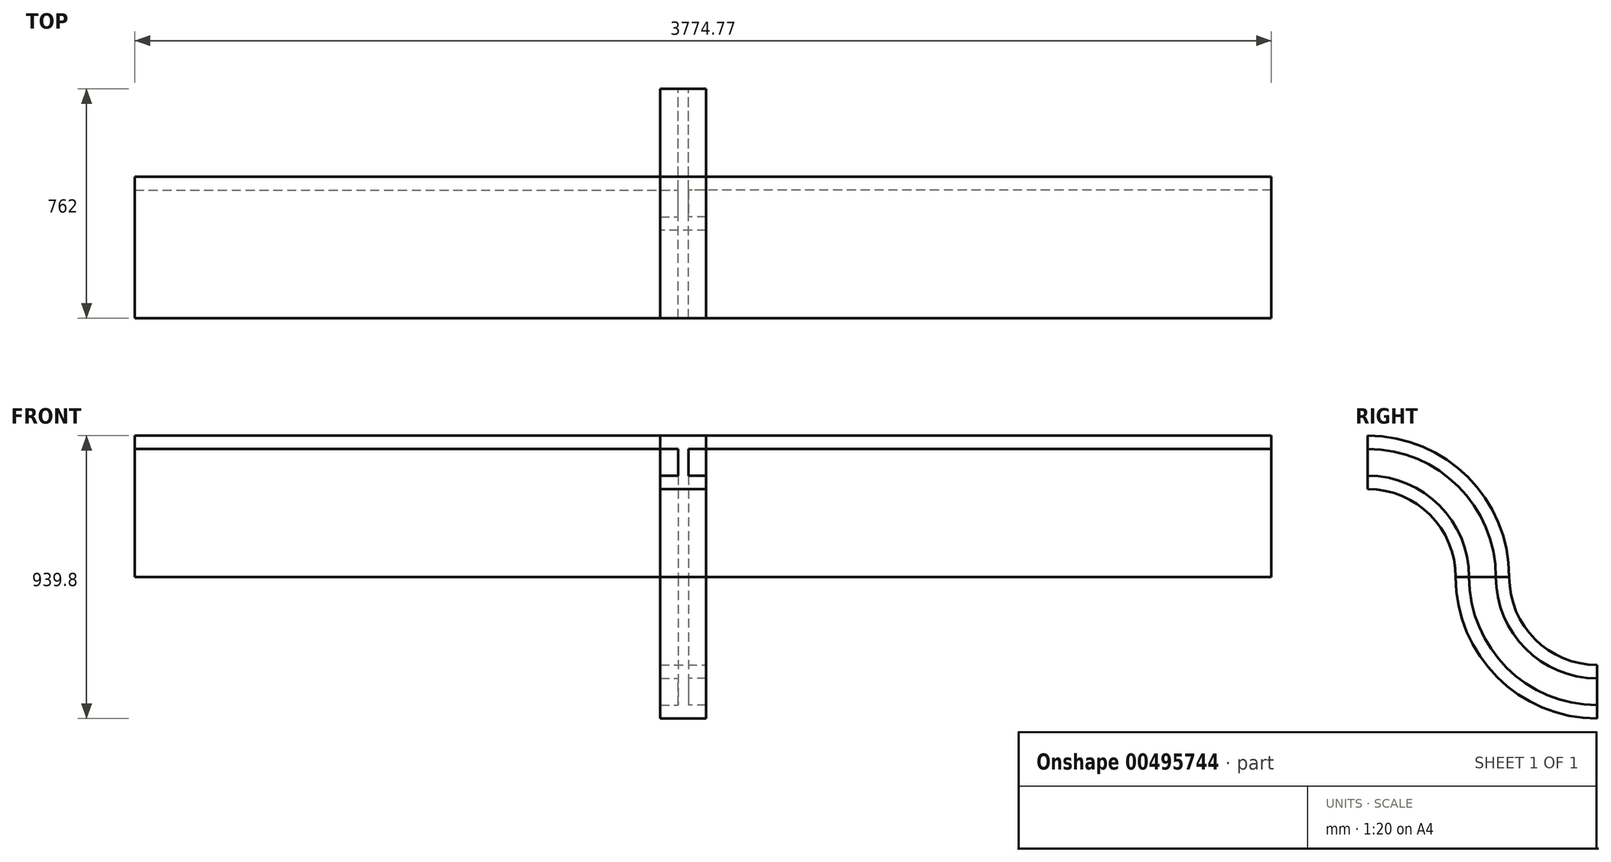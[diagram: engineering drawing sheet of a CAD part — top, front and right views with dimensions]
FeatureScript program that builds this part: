
annotation { "Feature Type Name" : "Feature", "Feature Type Description" : "" }
export const myFeature = defineFeature(function(context is Context, id is Id, definition is map)
    precondition{}
    {
        {
            var Q0;
            Q0=qCreatedBy(makeId("Front.planeOp"),FACE);
            var sketch = newSketch(context, id + "F0", { "sketchPlane" : qUnion([Q0])});
            skLineSegment(sketch, "E0", {"start": v(0, 88.9) * mm, "end": v(76.2, 88.9) * mm});
            skLineSegment(sketch, "E1", {"start": v(76.2, 88.9) * mm, "end": v(76.2, 44.45) * mm});
            skLineSegment(sketch, "E2", {"start": v(76.2, 44.45) * mm, "end": v(17.37, 44.45) * mm});
            skLineSegment(sketch, "E3", {"start": v(0, 88.9) * mm, "end": v(0, -88.9) * mm, "construction": true});
            skLineSegment(sketch, "E4", {"start": v(-17.37, 0) * mm, "end": v(17.37, 0) * mm, "construction": true});
            skLineSegment(sketch, "E5", {"start": v(17.37, 0) * mm, "end": v(17.37, 44.45) * mm});
            skLineSegment(sketch, "E6.MirrorCS", {"start": v(0, 88.9) * mm, "end": v(-76.2, 88.9) * mm});
            skLineSegment(sketch, "E7.MirrorCS", {"start": v(-76.2, 88.9) * mm, "end": v(-76.2, 44.45) * mm});
            skLineSegment(sketch, "E8.MirrorCS", {"start": v(-17.37, 0) * mm, "end": v(-17.37, 44.45) * mm});
            skLineSegment(sketch, "E9.MirrorCS", {"start": v(-76.2, 44.45) * mm, "end": v(-17.37, 44.45) * mm});
            skLineSegment(sketch, "E10.MirrorCS", {"start": v(0, -88.9) * mm, "end": v(-76.2, -88.9) * mm});
            skLineSegment(sketch, "E11.MirrorCS", {"start": v(-76.2, -88.9) * mm, "end": v(-76.2, -44.45) * mm});
            skLineSegment(sketch, "E12.MirrorCS", {"start": v(-76.2, -44.45) * mm, "end": v(-17.37, -44.45) * mm});
            skLineSegment(sketch, "E13.MirrorCS", {"start": v(-17.37, 0) * mm, "end": v(-17.37, -44.45) * mm});
            skLineSegment(sketch, "E14.MirrorCS", {"start": v(76.2, -44.45) * mm, "end": v(17.37, -44.45) * mm});
            skLineSegment(sketch, "E15.MirrorCS", {"start": v(0, -88.9) * mm, "end": v(76.2, -88.9) * mm});
            skLineSegment(sketch, "E16.MirrorCS", {"start": v(17.37, 0) * mm, "end": v(17.37, -44.45) * mm});
            skLineSegment(sketch, "E17.MirrorCS", {"start": v(76.2, -88.9) * mm, "end": v(76.2, -44.45) * mm});
            skSolve(sketch);
        }
        {
            var Q0;
            Q0=qCreatedBy(makeId("Right.planeOp"),FACE);
            var sketch = newSketch(context, id + "F1", { "sketchPlane" : qUnion([Q0])});
            skArc(sketch, "E18", {"start": v(0, 0) * mm, "mid": v(269.4, -111.6) * mm, "end": v(381, -381) * mm});
            skArc(sketch, "E19", {"start": v(381, -381) * mm, "mid": v(492.6, -650.4) * mm, "end": v(762, -762) * mm});
            skSolve(sketch);
        }
        {
            var Q0;
            Q0=makeQuery(id+"F0.imprint","IMPRINT",FACE,{"disambiguationData":[TD([[makeQuery(id+"F0.imprint","IMPRINT",EDGE,{"derivedFrom":sQuery(id+"F0.wireOp",EDGE,"E0")}),-1.0]])]});
            var Q1;
            Q1=sQuery(id+"F1.wireOp",EDGE,"E18");
            sweep(context, id + "F2", {"profiles" : qUnion([Q0]), "path" : qUnion([Q1])});
        }
        {
            var Q0;
            Q0=makeQuery(id+"F2.opSweep","SWEPT_FACE",FACE,{"disambiguationData":[OSD([sQuery(id+"F0.wireOp",EDGE,"E7.MirrorCS"),sQuery(id+"F1.wireOp",EDGE,"E18")])]});
            var sketch = newSketch(context, id + "F3", { "sketchPlane" : qUnion([Q0])});
            skSolve(sketch);
        }
        {
            var Q0;
            Q0=makeQuery(id+"F2.opSweep","SWEPT_FACE",FACE,{"disambiguationData":[OSD([sQuery(id+"F0.wireOp",EDGE,"E1"),sQuery(id+"F1.wireOp",EDGE,"E18")])]});
            extrude(context, id + "F4", {"entities" : qUnion([Q0]), "operationType" : NewBodyOperationType.ADD, "depth" : 1877.23 * mm});
        }
        {
            var Q0;
            {var subQ1=sQuery(id+"F0.wireOp",EDGE,"E7.MirrorCS");Q0=makeQuery(id+"F3.imprint","IMPRINT",FACE,{"disambiguationData":[TD([[makeQuery(id+"F3.imprint","IMPRINT",EDGE,{"derivedFrom":makeQuery(id+"F2.opSweep","CAP_EDGE",EDGE,{"disambiguationData":[OSD([subQ1,sQuery(id+"F1.wireOp",VERTEX,"E18.start")])],"isStart":true})}),1.0]])]});}
            extrude(context, id + "F5", {"entities" : qUnion([Q0]), "operationType" : NewBodyOperationType.ADD, "depth" : 1745.14 * mm});
        }
        {
            var Q0;
            Q0=makeQuery(id+"F0.imprint","IMPRINT",FACE,{"disambiguationData":[TD([[makeQuery(id+"F0.imprint","IMPRINT",EDGE,{"derivedFrom":sQuery(id+"F0.wireOp",EDGE,"E0")}),-1.0]])]});
            var Q1;
            Q1=sQuery(id+"F1.wireOp",EDGE,"E18");
            var Q2;
            Q2=sQuery(id+"F1.wireOp",EDGE,"E19");
            sweep(context, id + "F6", {"profiles" : qUnion([Q0]), "path" : qUnion([Q1, Q2])});
        }
    });
